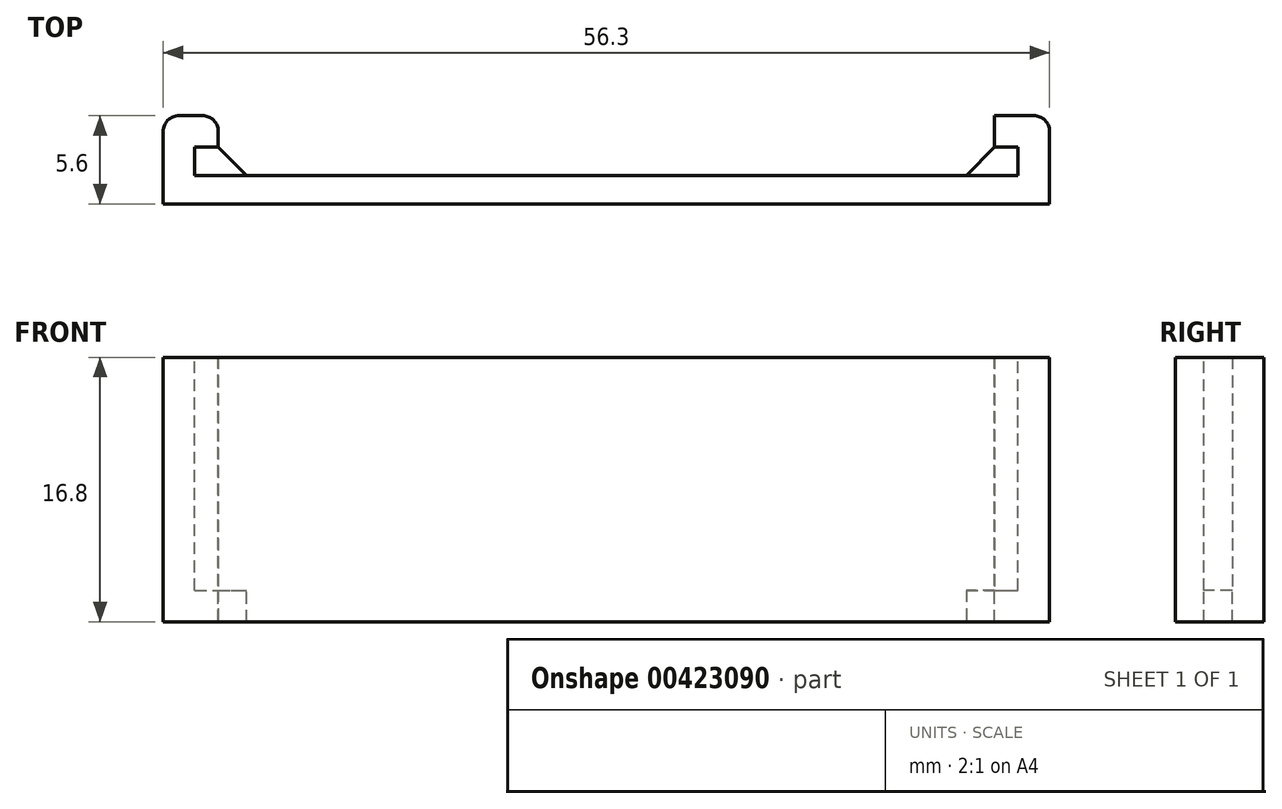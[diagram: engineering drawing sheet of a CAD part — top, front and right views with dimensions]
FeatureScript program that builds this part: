
annotation { "Feature Type Name" : "Feature", "Feature Type Description" : "" }
export const myFeature = defineFeature(function(context is Context, id is Id, definition is map)
    precondition{}
    {
        {
            var Q0;
            Q0=qCreatedBy(makeId("Top.planeOp"),FACE);
            var sketch = newSketch(context, id + "F0", { "sketchPlane" : qUnion([Q0])});
            skLineSegment(sketch, "E0.bottom", {"start": v(0, 0) * mm, "end": v(52.3, 0) * mm});
            skLineSegment(sketch, "E0.top", {"start": v(0, 1.8) * mm, "end": v(52.3, 1.8) * mm});
            skLineSegment(sketch, "E0.left", {"start": v(0, 0) * mm, "end": v(0, 1.8) * mm});
            skLineSegment(sketch, "E0.right", {"start": v(52.3, 0) * mm, "end": v(52.3, 1.8) * mm});
            skSolve(sketch);
        }
        {
            var Q0;
            Q0=makeQuery(id+"F0.imprint","IMPRINT",FACE,{"disambiguationData":[TD([[makeQuery(id+"F0.imprint","IMPRINT",EDGE,{"derivedFrom":sQuery(id+"F0.wireOp",EDGE,"E0.bottom")}),1.0]])]});
            extrude(context, id + "F1", {"entities" : qUnion([Q0]), "oppositeDirection" : true, "depth" : 14.8 * mm, "offsetDistance" : 25 * mm});
        }
        {
            var Q0;
            Q0=makeQuery(id+"F1.opExtrude","CAP_FACE",FACE,{"disambiguationData":[OSD([sQuery(id+"F0.wireOp",EDGE,"E0.bottom"),sQuery(id+"F0.wireOp",EDGE,"E0.top"),sQuery(id+"F0.wireOp",EDGE,"E0.left"),sQuery(id+"F0.wireOp",EDGE,"E0.right")])],"isStart":true});
            shell(context, id + "F2", {"entities" : qUnion([Q0]), "thickness" : 2 * mm, "oppositeDirection" : true});
        }
        {
            var Q0;
            Q0=makeQuery(id+"F1.opExtrude","CAP_FACE",FACE,{"disambiguationData":[OSD([sQuery(id+"F0.wireOp",EDGE,"E0.bottom"),sQuery(id+"F0.wireOp",EDGE,"E0.top"),sQuery(id+"F0.wireOp",EDGE,"E0.left"),sQuery(id+"F0.wireOp",EDGE,"E0.right")])],"isStart":true});
            var sketch = newSketch(context, id + "F3", { "sketchPlane" : qUnion([Q0])});
            skLineSegment(sketch, "E1", {"start": v(26.15, -2) * mm, "end": v(26.15, 3.8) * mm, "construction": true});
            skLineSegment(sketch, "E2.bottom", {"start": v(1.5, 3.8) * mm, "end": v(50.8, 3.8) * mm});
            skLineSegment(sketch, "E2.top", {"start": v(1.5, 1.8) * mm, "end": v(50.8, 1.8) * mm});
            skLineSegment(sketch, "E2.left", {"start": v(1.5, 3.8) * mm, "end": v(1.5, 1.8) * mm});
            skLineSegment(sketch, "E2.right", {"start": v(50.8, 3.8) * mm, "end": v(50.8, 1.8) * mm});
            skLineSegment(sketch, "E3.top", {"start": v(1.5, 0) * mm, "end": v(50.8, 0) * mm});
            skLineSegment(sketch, "E3.left", {"start": v(1.5, 1.8) * mm, "end": v(1.5, 0) * mm});
            skLineSegment(sketch, "E3.right", {"start": v(50.8, 1.8) * mm, "end": v(50.8, 0) * mm});
            skSolve(sketch);
        }
        {
            var Q0;
            Q0=makeQuery(id+"F3.imprint","IMPRINT",FACE,{"disambiguationData":[TD([[makeQuery(id+"F3.imprint","IMPRINT",EDGE,{"derivedFrom":sQuery(id+"F3.wireOp",EDGE,"E2.bottom")}),-1.0]])]});
            var Q1;
            Q1=makeQuery(id+"F3.imprint","IMPRINT",FACE,{"disambiguationData":[TD([[makeQuery(id+"F3.imprint","IMPRINT",EDGE,{"derivedFrom":sQuery(id+"F3.wireOp",EDGE,"E2.top")}),-1.0]])]});
            var Q2;
            Q2=makeQuery(id+"F1.opExtrude","CAP_FACE",FACE,{"disambiguationData":[OSD([sQuery(id+"F0.wireOp",EDGE,"E0.bottom"),sQuery(id+"F0.wireOp",EDGE,"E0.top"),sQuery(id+"F0.wireOp",EDGE,"E0.left"),sQuery(id+"F0.wireOp",EDGE,"E0.right")])],"isStart":false});
            extrude(context, id + "F4", {"entities" : qUnion([Q0, Q1]), "operationType" : NewBodyOperationType.REMOVE, "endBound" : BoundingType.UP_TO_SURFACE, "oppositeDirection" : true, "depth" : 13 * mm, "endBoundEntityFace" : qUnion([Q2]), "offsetDistance" : 25 * mm});
        }
        {
            var Q0;
            Q0=makeQuery(id+"F1.opExtrude","SWEPT_FACE",FACE,{"disambiguationData":[OSD([sQuery(id+"F0.wireOp",EDGE,"E0.bottom")])]});
            extrude(context, id + "F5", {"entities" : qUnion([Q0]), "operationType" : NewBodyOperationType.REMOVE, "oppositeDirection" : true, "depth" : 0.2 * mm, "offsetDistance" : 25 * mm});
        }
        {
            var Q0;
            Q0=makeQuery(id+"F4.boolean.opBoolean","COPY",EDGE,{"derivedFrom":makeQuery(id+"F4.opExtrude","SWEPT_EDGE",EDGE,{"disambiguationData":[OSD([sQuery(id+"F0.wireOp",EDGE,"E0.bottom"),sQuery(id+"F3.wireOp",EDGE,"E3.top"),sQuery(id+"F3.wireOp",EDGE,"E3.left")])]})});
            var Q1;
            Q1=makeQuery(id+"F4.boolean.opBoolean","COPY",EDGE,{"derivedFrom":makeQuery(id+"F4.opExtrude","SWEPT_EDGE",EDGE,{"disambiguationData":[OSD([sQuery(id+"F0.wireOp",EDGE,"E0.bottom"),sQuery(id+"F3.wireOp",EDGE,"E3.top"),sQuery(id+"F3.wireOp",EDGE,"E3.right")])]})});
            chamfer(context, id + "F6", {"entities" : qUnion([Q0, Q1]), "width" : 1.8 * mm, "tangentPropagation" : true});
        }
        {
            var Q0;
            Q0=makeQuery(id+"F4.boolean.opBoolean","COPY",EDGE,{"derivedFrom":makeQuery(id+"F4.opExtrude","SWEPT_EDGE",EDGE,{"disambiguationData":[OSD([sQuery(id+"F0.wireOp",EDGE,"E0.top"),sQuery(id+"F3.wireOp",EDGE,"E2.bottom"),sQuery(id+"F3.wireOp",EDGE,"E2.left")])]})});
            var Q1;
            Q1=makeQuery(id+"F1.opExtrude","SWEPT_EDGE",EDGE,{"disambiguationData":[OSD([sQuery(id+"F0.wireOp",EDGE,"E0.top"),sQuery(id+"F0.wireOp",EDGE,"E0.left")])]});
            var Q2;
            Q2=makeQuery(id+"F5.boolean.opBoolean","COPY",EDGE,{"derivedFrom":makeQuery(id+"F5.opExtrude","CAP_EDGE",EDGE,{"disambiguationData":[OSD([sQuery(id+"F0.wireOp",EDGE,"E0.bottom"),sQuery(id+"F0.wireOp",EDGE,"E0.left")])],"isStart":false})});
            var Q3;
            Q3=makeQuery(id+"F5.boolean.opBoolean","COPY",EDGE,{"derivedFrom":makeQuery(id+"F5.opExtrude","CAP_EDGE",EDGE,{"disambiguationData":[OSD([sQuery(id+"F0.wireOp",EDGE,"E0.bottom"),sQuery(id+"F0.wireOp",EDGE,"E0.right")])],"isStart":false})});
            var Q4;
            Q4=makeQuery(id+"F1.opExtrude","SWEPT_EDGE",EDGE,{"disambiguationData":[OSD([sQuery(id+"F0.wireOp",EDGE,"E0.top"),sQuery(id+"F0.wireOp",EDGE,"E0.right")])]});
            var Q5;
            Q5=makeQuery(id+"F4.boolean.opBoolean","COPY",EDGE,{"derivedFrom":makeQuery(id+"F4.opExtrude","SWEPT_EDGE",EDGE,{"disambiguationData":[OSD([sQuery(id+"F0.wireOp",EDGE,"E0.top"),sQuery(id+"F3.wireOp",EDGE,"E2.bottom"),sQuery(id+"F3.wireOp",EDGE,"E2.right")])]})});
            fillet(context, id + "F7", {"entities" : qUnion([Q0, Q1, Q2, Q3, Q4, Q5]), "tangentPropagation" : true, "radius" : 1 * mm, "defaultsChanged" : true, "vertexSettings" : [], "allowEdgeOverflow" : false});
        }
    });
